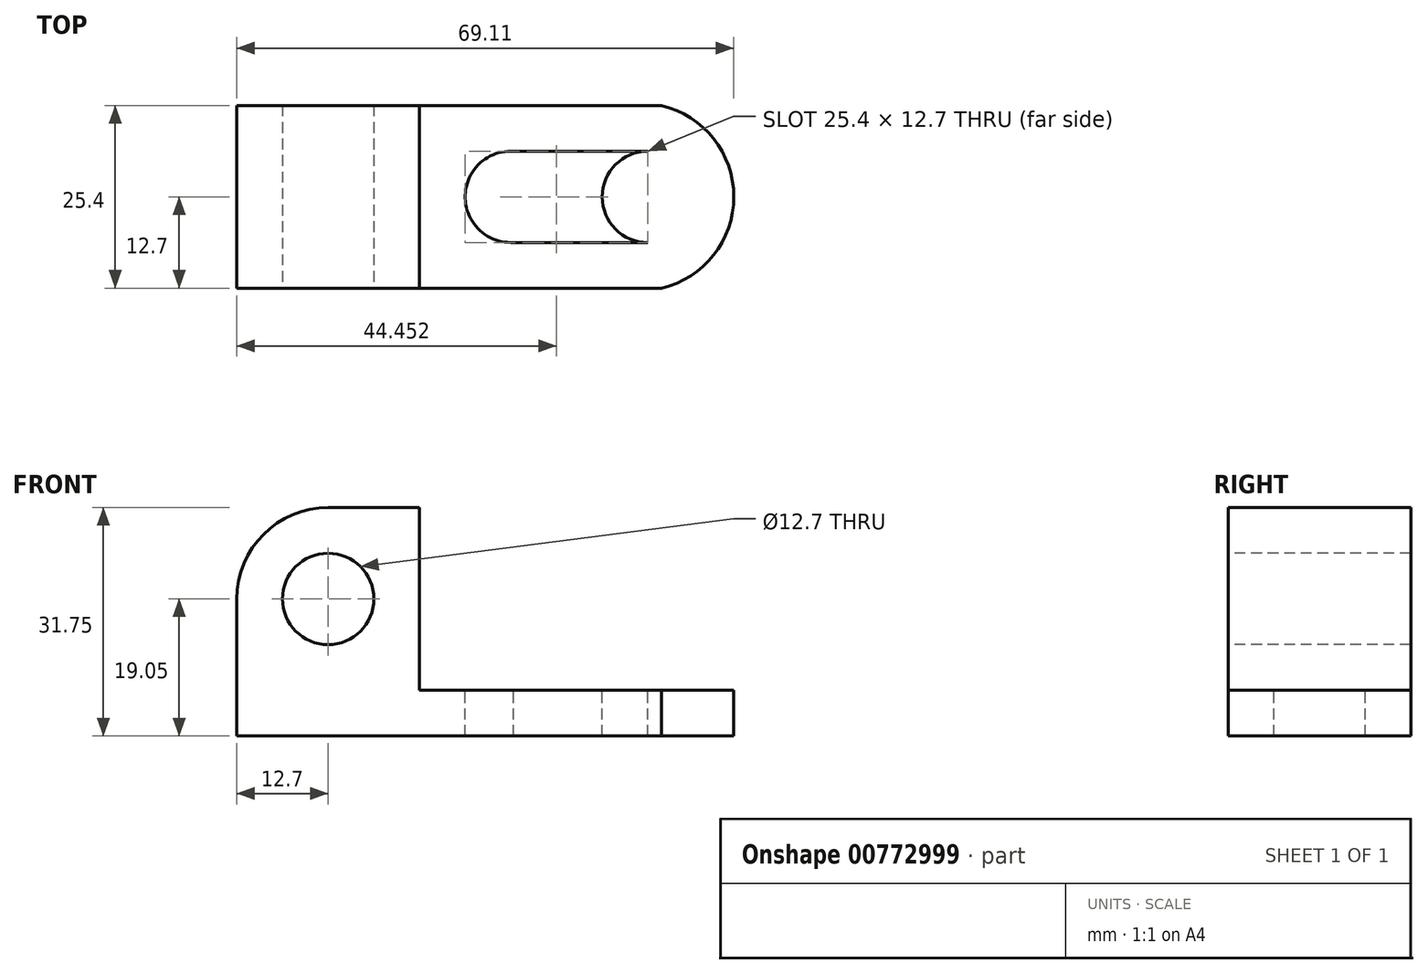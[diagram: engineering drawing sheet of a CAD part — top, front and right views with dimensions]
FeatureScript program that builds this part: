
annotation { "Feature Type Name" : "Feature", "Feature Type Description" : "" }
export const myFeature = defineFeature(function(context is Context, id is Id, definition is map)
    precondition{}
    {
        {
            var Q0;
            Q0=qCreatedBy(makeId("Front.planeOp"),FACE);
            var sketch = newSketch(context, id + "F0", { "sketchPlane" : qUnion([Q0])});
            skLineSegment(sketch, "E0", {"start": v(0, 0) * mm, "end": v(69.85, 0) * mm});
            skLineSegment(sketch, "E1", {"start": v(69.85, 0) * mm, "end": v(69.85, 31.75) * mm});
            skLineSegment(sketch, "E2", {"start": v(69.85, 31.75) * mm, "end": v(0, 31.75) * mm});
            skLineSegment(sketch, "E3", {"start": v(0, 31.75) * mm, "end": v(0, 0) * mm});
            skSolve(sketch);
        }
        {
            var Q0;
            Q0=makeQuery(id+"F0.imprint","IMPRINT",FACE,{"disambiguationData":[TD([[makeQuery(id+"F0.imprint","IMPRINT",EDGE,{"derivedFrom":sQuery(id+"F0.wireOp",EDGE,"E0")}),1.0]])]});
            extrude(context, id + "F1", {"entities" : qUnion([Q0]), "depth" : 25.4 * mm, "offsetDistance" : 25.4 * mm});
        }
        {
            var Q0;
            Q0=makeQuery(id+"F1.opExtrude","CAP_FACE",FACE,{"disambiguationData":[OSD([sQuery(id+"F0.wireOp",EDGE,"E0"),sQuery(id+"F0.wireOp",EDGE,"E1"),sQuery(id+"F0.wireOp",EDGE,"E2"),sQuery(id+"F0.wireOp",EDGE,"E3")])],"isStart":false});
            var sketch = newSketch(context, id + "F2", { "sketchPlane" : qUnion([Q0])});
            skLineSegment(sketch, "E4", {"start": v(25.4, 31.75) * mm, "end": v(25.4, 6.35) * mm});
            skLineSegment(sketch, "E5", {"start": v(25.4, 6.35) * mm, "end": v(69.85, 6.35) * mm});
            skLineSegment(sketch, "E6", {"start": v(69.85, 6.35) * mm, "end": v(69.85, 31.75) * mm});
            skLineSegment(sketch, "E7", {"start": v(69.85, 31.75) * mm, "end": v(25.4, 31.75) * mm});
            skSolve(sketch);
        }
        {
            var Q0;
            Q0=makeQuery(id+"F2.imprint","IMPRINT",FACE,{"disambiguationData":[TD([[makeQuery(id+"F2.imprint","IMPRINT",EDGE,{"derivedFrom":sQuery(id+"F2.wireOp",EDGE,"E4")}),1.0]])]});
            extrude(context, id + "F3", {"entities" : qUnion([Q0]), "operationType" : NewBodyOperationType.REMOVE, "oppositeDirection" : true, "depth" : 25.4 * mm, "offsetDistance" : 25.4 * mm});
        }
        {
            var Q0;
            Q0=makeQuery(id+"F3.boolean.opBoolean","COPY",EDGE,{"derivedFrom":makeQuery(id+"F3.opExtrude","SWEPT_EDGE",EDGE,{"disambiguationData":[OSD([sQuery(id+"F0.wireOp",EDGE,"E2"),sQuery(id+"F2.wireOp",EDGE,"E4"),sQuery(id+"F2.wireOp",EDGE,"E7")])]})});
            var Q1;
            Q1=makeQuery(id+"F1.opExtrude","SWEPT_EDGE",EDGE,{"disambiguationData":[OSD([sQuery(id+"F0.wireOp",EDGE,"E2"),sQuery(id+"F0.wireOp",EDGE,"E3")])]});
            fillet(context, id + "F4", {"entities" : qUnion([Q0, Q1]), "radius" : 12.7 * mm, "tangentPropagation" : true, "allowEdgeOverflow" : false});
        }
        {
            var Q0;
            Q0=makeQuery(id+"F3.boolean.opBoolean","COPY",FACE,{"derivedFrom":makeQuery(id+"F3.opExtrude","SWEPT_FACE",FACE,{"disambiguationData":[OSD([sQuery(id+"F2.wireOp",EDGE,"E5")])]})});
            var sketch = newSketch(context, id + "F5", { "sketchPlane" : qUnion([Q0])});
            skCircle(sketch, "E8", {"center": v(38.1, -12.7) * mm, "radius": 6.35 * mm});
            skSolve(sketch);
        }
        {
            var Q0;
            Q0=makeQuery(id+"F5.imprint","IMPRINT",FACE,{"disambiguationData":[TD([[makeQuery(id+"F5.imprint","IMPRINT",EDGE,{"derivedFrom":sQuery(id+"F5.wireOp",EDGE,"E8")}),-1.0]])]});
            var sketch = newSketch(context, id + "F6", { "sketchPlane" : qUnion([Q0])});
            skCircle(sketch, "E9", {"center": v(57.15, -12.7) * mm, "radius": 6.35 * mm});
            skLineSegment(sketch, "E10", {"start": v(57.15, -6.35) * mm, "end": v(37.88, -6.35) * mm});
            skLineSegment(sketch, "E11", {"start": v(37.88, -19.04) * mm, "end": v(57.15, -19.05) * mm});
            skSolve(sketch);
        }
        {
            var Q0;
            Q0=makeQuery(id+"F5.imprint","IMPRINT",FACE,{"disambiguationData":[TD([[makeQuery(id+"F5.imprint","IMPRINT",EDGE,{"derivedFrom":sQuery(id+"F5.wireOp",EDGE,"E8")}),1.0]])]});
            extrude(context, id + "F7", {"entities" : qUnion([Q0]), "operationType" : NewBodyOperationType.REMOVE, "oppositeDirection" : true, "depth" : 25.4 * mm, "offsetDistance" : 25.4 * mm});
        }
        {
            var Q0;
            {var subQ0=sQuery(id+"F6.wireOp",EDGE,"E10");var subQ1=sQuery(id+"F6.wireOp",EDGE,"E9");var subQ2=makeQuery(id+"F6.imprint","INTERSECT",VERTEX,{"derivedFrom":[subQ1,subQ0]});Q0=makeQuery(id+"F6.imprint","IMPRINT",FACE,{"disambiguationData":[TD([[makeQuery(id+"F6.imprint","IMPRINT",EDGE,{"disambiguationData":[TD([[subQ2,-1.0]])],"derivedFrom":subQ1}),-1.0]])]});}
            var Q1;
            {var subQ0=sQuery(id+"F6.wireOp",EDGE,"E9");var subQ3=makeQuery(id+"F6.imprint","IMPRINT",VERTEX,{"derivedFrom":subQ0});Q1=makeQuery(id+"F6.imprint","IMPRINT",FACE,{"disambiguationData":[TD([[makeQuery(id+"F6.imprint","IMPRINT",EDGE,{"disambiguationData":[TD([[subQ3,1.0]])],"derivedFrom":subQ0}),1.0]])]});}
            extrude(context, id + "F8", {"entities" : qUnion([Q0, Q1]), "operationType" : NewBodyOperationType.REMOVE, "oppositeDirection" : true, "depth" : 25.4 * mm, "offsetDistance" : 25.4 * mm});
        }
        {
            var Q0;
            Q0=makeQuery(id+"F3.boolean.opBoolean","COPY",FACE,{"derivedFrom":makeQuery(id+"F3.opExtrude","SWEPT_FACE",FACE,{"disambiguationData":[OSD([sQuery(id+"F2.wireOp",EDGE,"E5")])]})});
            var sketch = newSketch(context, id + "F9", { "sketchPlane" : qUnion([Q0])});
            skArc(sketch, "E12", {"start": v(64.38, -25.4) * mm, "mid": v(69.47, -12.59) * mm, "end": v(63.85, 0) * mm});
            skSolve(sketch);
        }
        {
            var Q0;
            {var subQ0=sQuery(id+"F9.wireOp",EDGE,"E12");Q0=makeQuery(id+"F9.imprint","IMPRINT",FACE,{"disambiguationData":[TD([[makeQuery(id+"F9.imprint","IMPRINT",EDGE,{"derivedFrom":subQ0}),-1.0]])]});}
            extrude(context, id + "F10", {"entities" : qUnion([Q0]), "operationType" : NewBodyOperationType.REMOVE, "oppositeDirection" : true, "depth" : 25.4 * mm, "offsetDistance" : 25.4 * mm});
        }
        {
            var Q0;
            Q0=makeQuery(id+"F1.opExtrude","CAP_FACE",FACE,{"disambiguationData":[OSD([sQuery(id+"F0.wireOp",EDGE,"E0"),sQuery(id+"F0.wireOp",EDGE,"E1"),sQuery(id+"F0.wireOp",EDGE,"E2"),sQuery(id+"F0.wireOp",EDGE,"E3")])],"isStart":false});
            var sketch = newSketch(context, id + "F11", { "sketchPlane" : qUnion([Q0])});
            skCircle(sketch, "E13", {"center": v(12.7, 19.05) * mm, "radius": 6.35 * mm});
            skSolve(sketch);
        }
        {
            var Q0;
            Q0=makeQuery(id+"F11.imprint","IMPRINT",FACE,{"disambiguationData":[TD([[makeQuery(id+"F11.imprint","IMPRINT",EDGE,{"derivedFrom":sQuery(id+"F11.wireOp",EDGE,"E13")}),1.0]])]});
            extrude(context, id + "F12", {"entities" : qUnion([Q0]), "operationType" : NewBodyOperationType.REMOVE, "oppositeDirection" : true, "depth" : 25.4 * mm, "offsetDistance" : 25.4 * mm});
        }
        {
            var Q0;
            Q0=makeQuery(id+"F3.boolean.opBoolean","COPY",FACE,{"derivedFrom":makeQuery(id+"F3.opExtrude","SWEPT_FACE",FACE,{"disambiguationData":[OSD([sQuery(id+"F2.wireOp",EDGE,"E5")])]})});
            var sketch = newSketch(context, id + "F13", { "sketchPlane" : qUnion([Q0])});
            skArc(sketch, "E14", {"start": v(59.08, -25.4) * mm, "mid": v(69.11, -12.7) * mm, "end": v(59.08, 0) * mm});
            skSolve(sketch);
        }
        {
            var Q0;
            {var subQ0=sQuery(id+"F13.wireOp",EDGE,"E14");Q0=makeQuery(id+"F13.imprint","IMPRINT",FACE,{"disambiguationData":[TD([[makeQuery(id+"F13.imprint","IMPRINT",EDGE,{"derivedFrom":subQ0}),-1.0]])]});}
            extrude(context, id + "F14", {"entities" : qUnion([Q0]), "operationType" : NewBodyOperationType.REMOVE, "oppositeDirection" : true, "depth" : 25.4 * mm, "offsetDistance" : 25.4 * mm});
        }
    });
